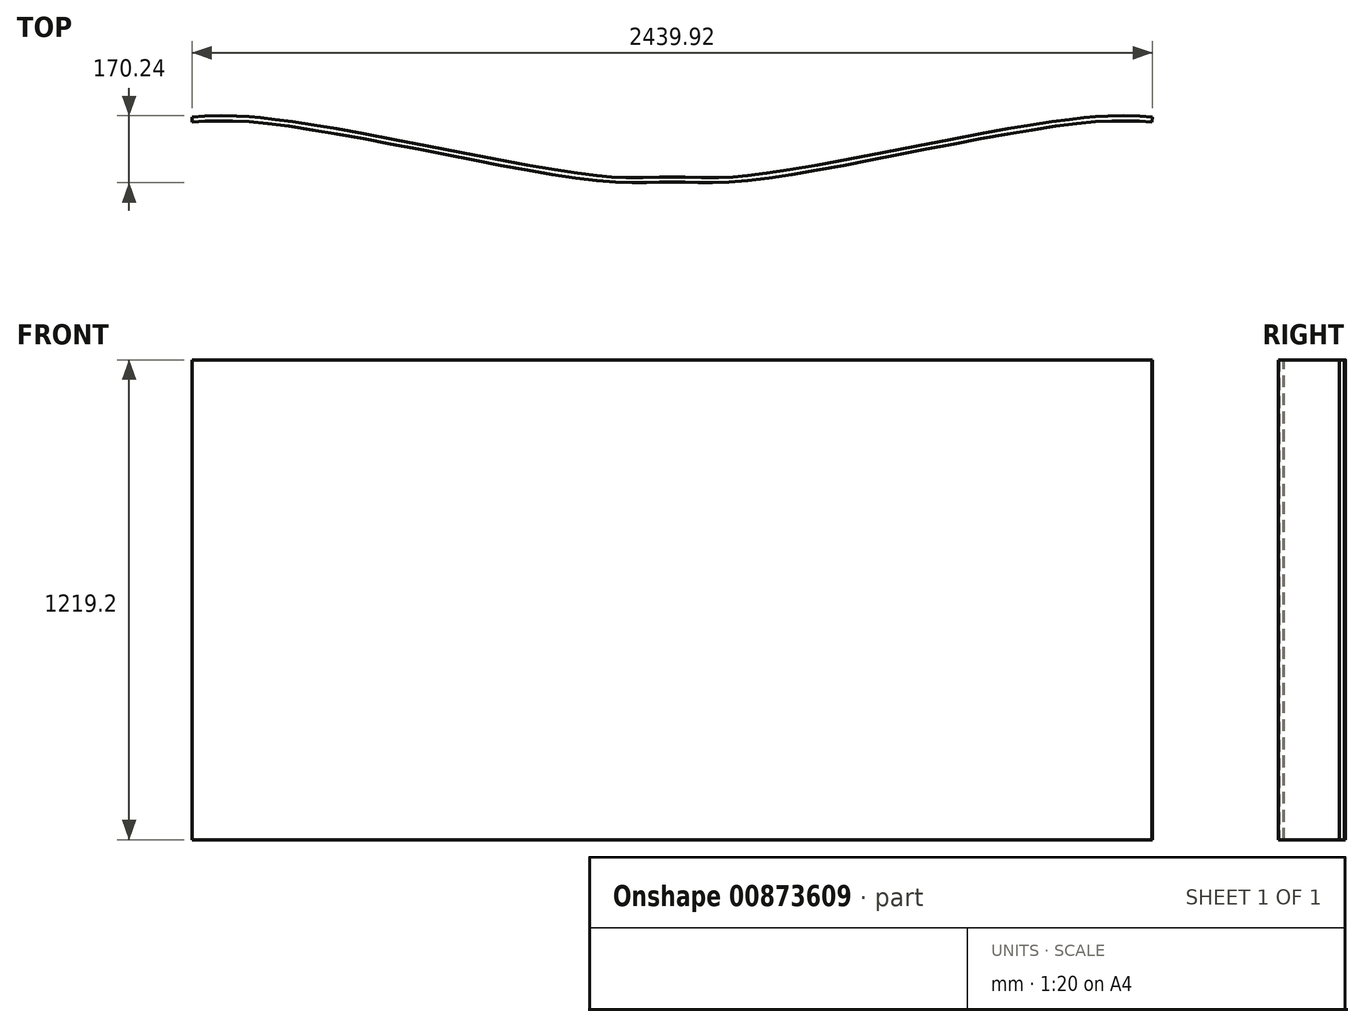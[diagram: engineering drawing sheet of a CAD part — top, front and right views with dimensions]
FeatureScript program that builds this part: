
annotation { "Feature Type Name" : "Feature", "Feature Type Description" : "" }
export const myFeature = defineFeature(function(context is Context, id is Id, definition is map)
    precondition{}
    {
        {
            var Q0;
            Q0=qCreatedBy(makeId("Top.planeOp"),FACE);
            var sketch = newSketch(context, id + "F0", { "sketchPlane" : qUnion([Q0])});
            skLineSegment(sketch, "E0.bottom", {"start": v(0, 0) * mm, "end": v(2438.4, 0) * mm, "construction": true});
            skLineSegment(sketch, "E0.top", {"start": v(0, 152.4) * mm, "end": v(2438.4, 152.4) * mm, "construction": true});
            skLineSegment(sketch, "E0.left", {"start": v(0, 0) * mm, "end": v(0, 152.4) * mm, "construction": true});
            skLineSegment(sketch, "E0.right", {"start": v(2438.4, 0) * mm, "end": v(2438.4, 152.4) * mm, "construction": true});
            skLineSegment(sketch, "E1", {"start": v(0, 76.2) * mm, "end": v(2682.13, 76.2) * mm, "construction": true});
            skLineSegment(sketch, "E2", {"start": v(1219.2, 152.4) * mm, "end": v(1219.2, -227.31) * mm, "construction": true});
            skLineSegment(sketch, "E3.1.0.0", {"start": v(1371.6, 152.4) * mm, "end": v(1371.6, -227.31) * mm, "construction": true});
            skLineSegment(sketch, "E3.2.0.0", {"start": v(1524, 152.4) * mm, "end": v(1524, -227.31) * mm, "construction": true});
            skLineSegment(sketch, "E3.3.0.0", {"start": v(1676.4, 152.4) * mm, "end": v(1676.4, -227.31) * mm, "construction": true});
            skLineSegment(sketch, "E3.direction1", {"start": v(1219.2, -227.31) * mm, "end": v(1371.6, -227.31) * mm, "construction": true});
            skLineSegment(sketch, "E4.0.4.0", {"start": v(1828.8, 152.4) * mm, "end": v(1828.8, -227.31) * mm, "construction": true});
            skLineSegment(sketch, "E4.0.5.0", {"start": v(1981.2, 152.4) * mm, "end": v(1981.2, -227.31) * mm, "construction": true});
            skLineSegment(sketch, "E4.0.6.0", {"start": v(2133.6, 152.4) * mm, "end": v(2133.6, -227.31) * mm, "construction": true});
            skLineSegment(sketch, "E4.0.7.0", {"start": v(2286, 152.4) * mm, "end": v(2286, -227.31) * mm, "construction": true});
            skLineSegment(sketch, "E5.0.8.0", {"start": v(2438.4, 152.4) * mm, "end": v(2438.4, -227.31) * mm, "construction": true});
            skFitSpline(sketch, "E6", {"points": [v(1219.2, 0) * mm, v(1371.6, 0) * mm, v(1828.8, 76.2) * mm, v(2286, 152.4) * mm, v(2438.4, 152.4) * mm], "startDerivative": vector(727.9, 0) * mm, "endDerivative": vector(726.6, -43.7) * mm});
            skFitSpline(sketch, "E7.MirrorCS", {"points": [v(1219.2, 0) * mm, v(1066.8, 0) * mm, v(609.6, 76.2) * mm, v(152.4, 152.4) * mm, v(0, 152.4) * mm], "startDerivative": vector(-727.9, 0) * mm, "endDerivative": vector(-726.6, -43.7) * mm});
            skFitSpline(sketch, "E8.0", {"points": [v(1219.2, 12.7) * mm, v(1211.47, 12.7) * mm, v(1196.1, 12.44) * mm, v(1172.7, 11.66) * mm, v(1148.32, 10.92) * mm, v(1122.32, 10.6) * mm, v(1098.73, 11.02) * mm, v(1078.37, 11.95) * mm, v(1062.29, 13) * mm, v(1045.28, 14.45) * mm, v(1021.47, 16.85) * mm, v(989.69, 20.72) * mm, v(948.7, 26.59) * mm, v(890.72, 35.83) * mm, v(812.94, 49.66) * mm, v(713.93, 68.62) * mm, v(612.06, 88.69) * mm, v(510.11, 108.6) * mm, v(427.43, 124.18) * mm, v(364.01, 135.5) * mm, v(318.16, 143.3) * mm, v(274.35, 150.25) * mm, v(239.84, 155.25) * mm, v(213.59, 158.7) * mm, v(194.62, 160.99) * mm, v(176.4, 162.97) * mm, v(161.9, 164.35) * mm, v(150.7, 165.29) * mm, v(139.8, 166.1) * mm, v(126.7, 166.93) * mm, v(111.73, 167.6) * mm, v(92.68, 168.15) * mm, v(70.4, 168.22) * mm, v(45.53, 167.57) * mm, v(22, 166.44) * mm, v(6.8, 165.53) * mm, v(-0.76, 165.08) * mm]});
            skFitSpline(sketch, "E8.1", {"points": [v(1219.2, 12.7) * mm, v(1226.93, 12.7) * mm, v(1242.3, 12.44) * mm, v(1265.7, 11.66) * mm, v(1290.08, 10.92) * mm, v(1316.08, 10.6) * mm, v(1339.67, 11.02) * mm, v(1360.03, 11.95) * mm, v(1376.11, 13) * mm, v(1393.12, 14.45) * mm, v(1416.93, 16.85) * mm, v(1448.71, 20.72) * mm, v(1489.7, 26.59) * mm, v(1547.68, 35.83) * mm, v(1625.46, 49.66) * mm, v(1724.47, 68.62) * mm, v(1826.34, 88.69) * mm, v(1928.29, 108.6) * mm, v(2010.97, 124.18) * mm, v(2074.39, 135.5) * mm, v(2120.24, 143.3) * mm, v(2164.05, 150.25) * mm, v(2198.56, 155.25) * mm, v(2224.81, 158.7) * mm, v(2243.78, 160.99) * mm, v(2262, 162.97) * mm, v(2276.5, 164.35) * mm, v(2287.7, 165.29) * mm, v(2298.6, 166.1) * mm, v(2311.7, 166.93) * mm, v(2326.67, 167.6) * mm, v(2345.72, 168.15) * mm, v(2368, 168.22) * mm, v(2392.87, 167.57) * mm, v(2416.4, 166.44) * mm, v(2431.6, 165.53) * mm, v(2439.16, 165.08) * mm]});
            skLineSegment(sketch, "E9", {"start": v(0, 152.4) * mm, "end": v(-0.76, 165.08) * mm});
            skLineSegment(sketch, "E10", {"start": v(2438.4, 152.4) * mm, "end": v(2439.16, 165.08) * mm});
            skSolve(sketch);
        }
        {
            var Q0;
            Q0 = qSketchRegion(id + "F0", true);
            var Q1;
            Q1=sQuery(id+"F0.wireOp",EDGE,"E0.top");
            var Q2;
            Q2=sQuery(id+"F0.wireOp",EDGE,"E0.bottom");
            var Q3;
            Q3=sQuery(id+"F0.wireOp",EDGE,"E0.left");
            var Q4;
            Q4=sQuery(id+"F0.wireOp",EDGE,"E0.right");
            var Q5;
            Q5=sQuery(id+"F0.wireOp",EDGE,"E7.MirrorCS");
            var Q6;
            Q6=sQuery(id+"F0.wireOp",EDGE,"E6");
            extrude(context, id + "F1", {"entities" : qUnion([Q0]), "surfaceEntities" : qUnion([Q1, Q2, Q3, Q4, Q5, Q6]), "depth" : 1219.2 * mm, "offsetDistance" : 25.4 * mm});
        }
    });
